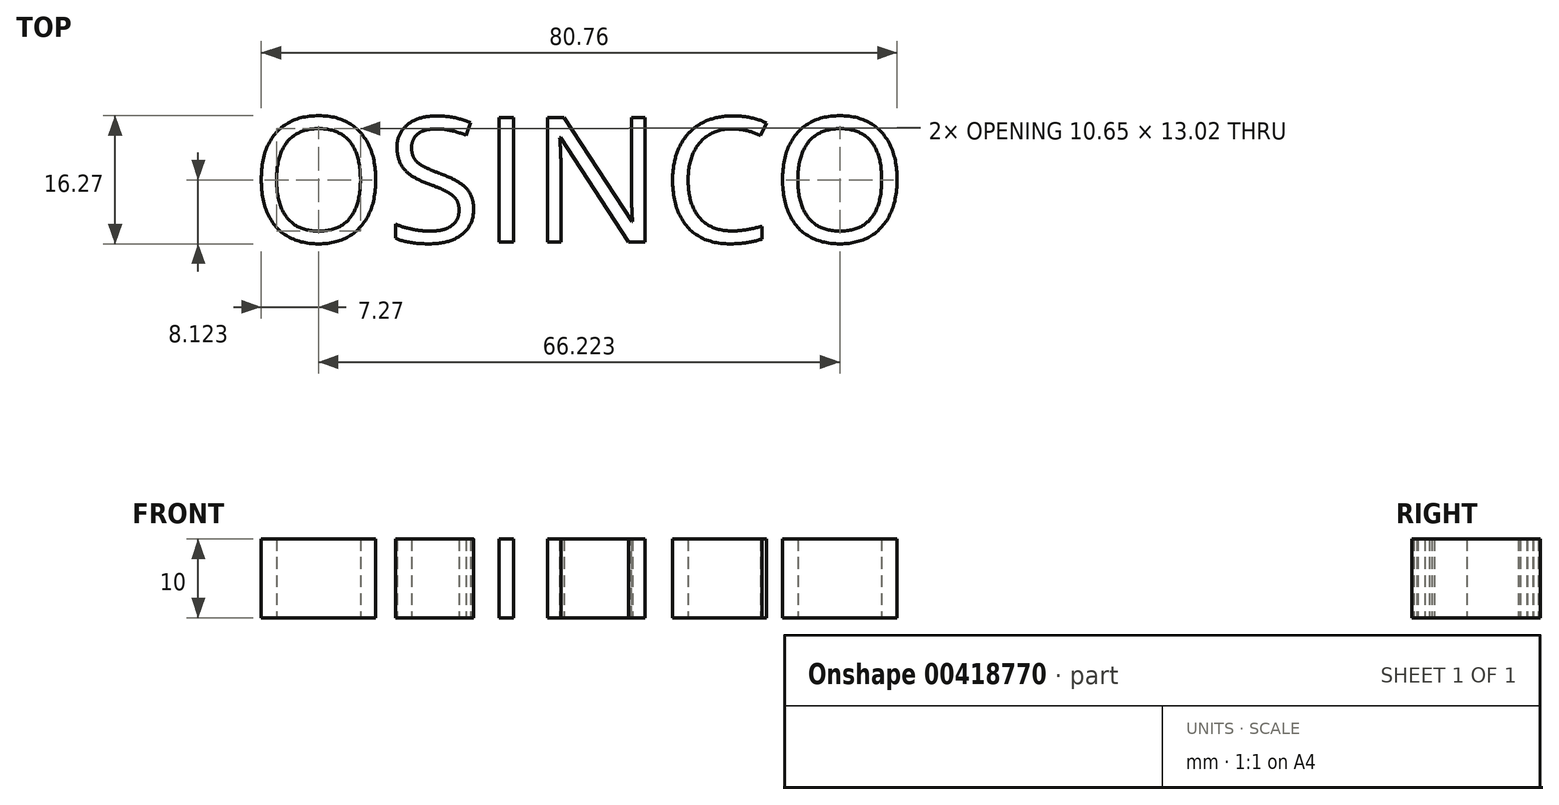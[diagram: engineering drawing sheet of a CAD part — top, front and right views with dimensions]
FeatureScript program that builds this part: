
annotation { "Feature Type Name" : "Feature", "Feature Type Description" : "" }
export const myFeature = defineFeature(function(context is Context, id is Id, definition is map)
    precondition{}
    {
        {
            var Q0;
            Q0=qCreatedBy(makeId("Top.planeOp"),FACE);
            var sketch = newSketch(context, id + "F0", { "sketchPlane" : qUnion([Q0])});
            skLineSegment(sketch, "E0.bottom", {"start": v(0, -34.53) * mm, "end": v(35.4, -34.53) * mm});
            skLineSegment(sketch, "E0.top", {"start": v(0, 0) * mm, "end": v(35.4, 0) * mm});
            skLineSegment(sketch, "E0.left", {"start": v(0, -34.53) * mm, "end": v(0, 0) * mm});
            skLineSegment(sketch, "E0.right", {"start": v(35.4, -34.53) * mm, "end": v(35.4, 0) * mm});
            skSolve(sketch);
        }
        {
            var Q0;
            Q0 = qSketchRegion(id + "F0", true);
            var sketch = newSketch(context, id + "F1", { "sketchPlane" : qUnion([Q0])});
            skText(sketch, "E1", { "text": "OSINCO", "fontName": "OpenSans-Regular.ttf"});
            const initialGuessF1  = {"E1": [0.0115, -0.0179, 1, 0, 0.01594]};
            skSetInitialGuess(sketch, initialGuessF1);
            skSolve(sketch);
        }
        {
            var Q0;
            Q0=makeQuery(id+"F1.imprint","IMPRINT",FACE,{"disambiguationData":[TD([[makeQuery(id+"F1.imprint","IMPRINT",EDGE,{"derivedFrom":sQuery(id+"F1.wireOp",EDGE,"E1.sketch_text.stroke-45")}),-1.0]])]});
            var Q1;
            Q1 = qSketchRegion(id + "F1", true);
            extrude(context, id + "F2", {"entities" : qUnion([Q0, Q1]), "depth" : 10 * mm});
        }
    });
